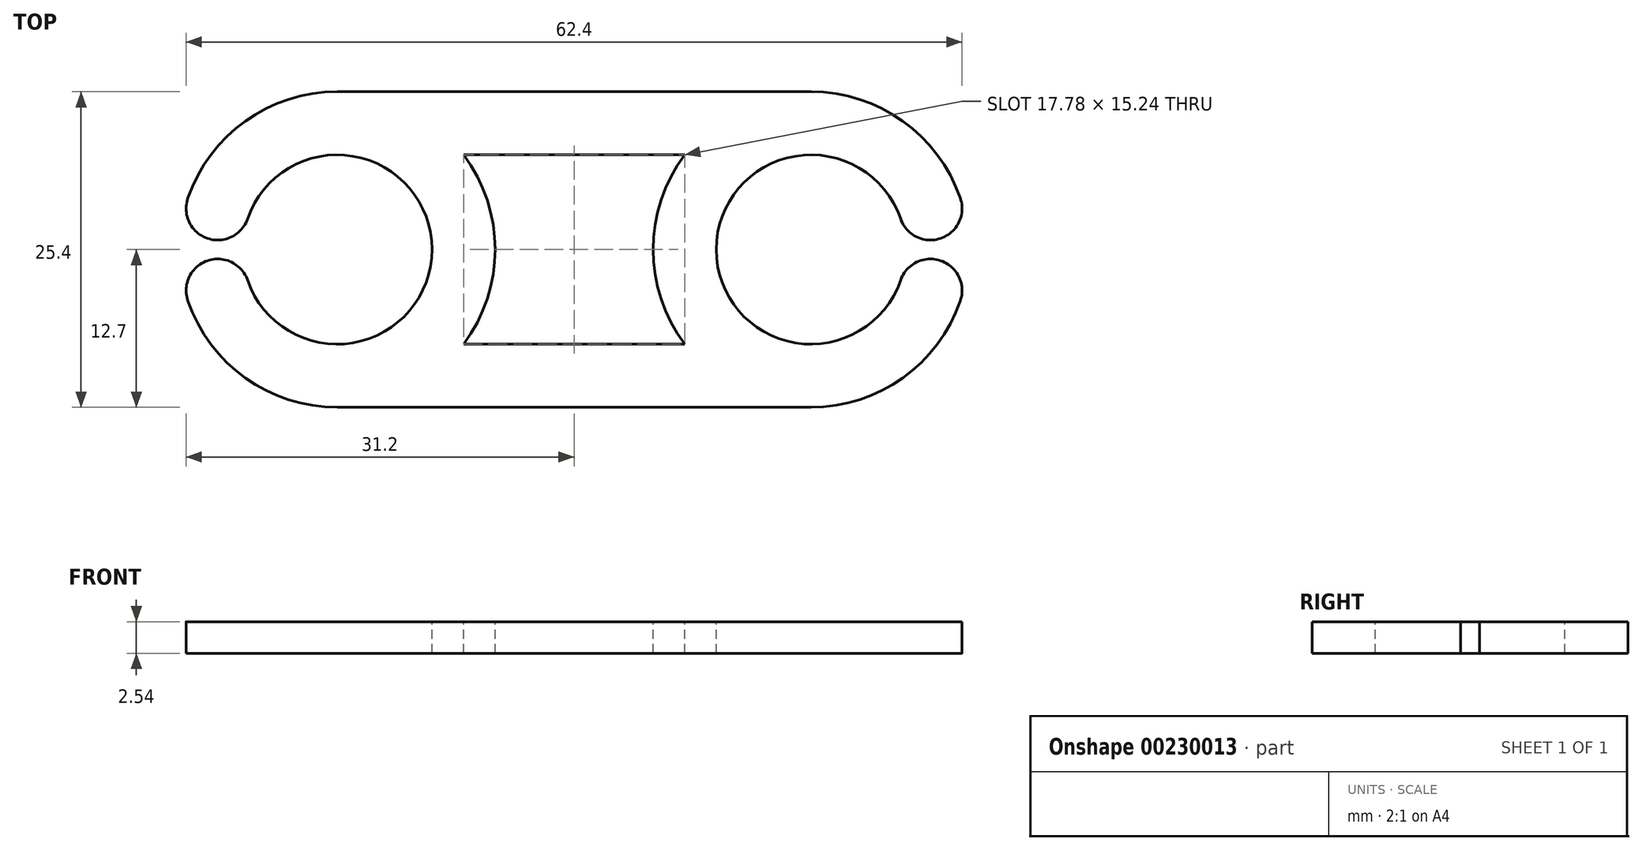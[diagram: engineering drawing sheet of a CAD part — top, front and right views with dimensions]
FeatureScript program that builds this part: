
annotation { "Feature Type Name" : "Feature", "Feature Type Description" : "" }
export const myFeature = defineFeature(function(context is Context, id is Id, definition is map)
    precondition{}
    {
        {
            var Q0;
            Q0=qCreatedBy(makeId("Top.planeOp"),FACE);
            var sketch = newSketch(context, id + "F0", { "sketchPlane" : qUnion([Q0])});
            skArc(sketch, "E0", {"start": v(-19.05, 12.7) * mm, "mid": v(-31.75, 0) * mm, "end": v(-19.05, -12.7) * mm});
            skArc(sketch, "E1", {"start": v(19.05, -12.7) * mm, "mid": v(31.75, 0) * mm, "end": v(19.05, 12.7) * mm});
            skLineSegment(sketch, "E2", {"start": v(-19.05, 12.7) * mm, "end": v(19.05, 12.7) * mm});
            skLineSegment(sketch, "E3", {"start": v(-19.05, -12.7) * mm, "end": v(19.05, -12.7) * mm});
            skLineSegment(sketch, "E4", {"start": v(-19.05, 12.7) * mm, "end": v(-19.05, -12.7) * mm, "construction": true});
            skLineSegment(sketch, "E5", {"start": v(19.05, 12.7) * mm, "end": v(19.05, -12.7) * mm, "construction": true});
            skLineSegment(sketch, "E6", {"start": v(0, 12.7) * mm, "end": v(0, -12.7) * mm, "construction": true});
            skSolve(sketch);
        }
        {
            var Q0;
            Q0 = qSketchRegion(id + "F0", true);
            extrude(context, id + "F1", {"entities" : qUnion([Q0]), "endBound" : BoundingType.SYMMETRIC, "depth" : 2.54 * mm});
        }
        {
            var Q0;
            Q0=makeQuery(id+"F1.opExtrude","CAP_FACE",FACE,{"disambiguationData":[OSD([sQuery(id+"F0.wireOp",EDGE,"E0"),sQuery(id+"F0.wireOp",EDGE,"E1"),sQuery(id+"F0.wireOp",EDGE,"E2"),sQuery(id+"F0.wireOp",EDGE,"E3")])],"isStart":false});
            var sketch = newSketch(context, id + "F2", { "sketchPlane" : qUnion([Q0])});
            skCircle(sketch, "E7", {"center": v(-19.05, 0) * mm, "radius": 7.62 * mm});
            skCircle(sketch, "E8", {"center": v(19.05, 0) * mm, "radius": 7.62 * mm});
            skLineSegment(sketch, "E9", {"start": v(-8.89, 7.62) * mm, "end": v(8.89, 7.62) * mm});
            skLineSegment(sketch, "E10", {"start": v(8.9, -7.62) * mm, "end": v(-8.9, -7.62) * mm});
            skArc(sketch, "E11", {"start": v(8.89, 7.62) * mm, "mid": v(6.35, 0) * mm, "end": v(8.9, -7.62) * mm});
            skArc(sketch, "E12", {"start": v(-8.9, -7.62) * mm, "mid": v(-6.35, 0) * mm, "end": v(-8.89, 7.62) * mm});
            skSolve(sketch);
        }
        {
            var Q0;
            Q0 = qSketchRegion(id + "F2", true);
            extrude(context, id + "F3", {"entities" : qUnion([Q0]), "operationType" : NewBodyOperationType.REMOVE, "oppositeDirection" : true, "depth" : 25.4 * mm});
        }
        {
            var Q0;
            Q0=makeQuery(id+"F1.opExtrude","CAP_FACE",FACE,{"disambiguationData":[OSD([sQuery(id+"F0.wireOp",EDGE,"E0"),sQuery(id+"F0.wireOp",EDGE,"E1"),sQuery(id+"F0.wireOp",EDGE,"E2"),sQuery(id+"F0.wireOp",EDGE,"E3")])],"isStart":false});
            var sketch = newSketch(context, id + "F4", { "sketchPlane" : qUnion([Q0])});
            skCircle(sketch, "E13", {"center": v(0, 0) * mm, "radius": 11.43 * mm});
            skCircle(sketch, "E14", {"center": v(0, 0) * mm, "radius": 6.35 * mm});
            skSolve(sketch);
        }
        {
            var Q0;
            Q0=makeQuery(id+"FMwU1qSj6TiMdTW_1.boolean.opBoolean","MERGE",FACE,{"derivedFrom":[makeQuery(id+"F1.opExtrude","CAP_FACE",FACE,{"disambiguationData":[OSD([sQuery(id+"F0.wireOp",EDGE,"E0"),sQuery(id+"F0.wireOp",EDGE,"E1"),sQuery(id+"F0.wireOp",EDGE,"E2"),sQuery(id+"F0.wireOp",EDGE,"E3")])],"isStart":false}),makeQuery(id+"FMwU1qSj6TiMdTW_1.opExtrude","CAP_FACE",FACE,{"disambiguationData":[OSD([sQuery(id+"F4.wireOp",EDGE,"E13"),sQuery(id+"F4.wireOp",EDGE,"E14")])],"isStart":true})]});
            var sketch = newSketch(context, id + "F5", { "sketchPlane" : qUnion([Q0])});
            skLineSegment(sketch, "E15.bottom", {"start": v(-19.21, 0.76) * mm, "end": v(-31.75, 0.76) * mm});
            skLineSegment(sketch, "E15.top", {"start": v(-19.21, -0.76) * mm, "end": v(-31.75, -0.76) * mm});
            skLineSegment(sketch, "E15.left", {"start": v(-19.21, 0.76) * mm, "end": v(-19.21, -0.76) * mm});
            skLineSegment(sketch, "E15.right", {"start": v(-31.75, 0.76) * mm, "end": v(-31.75, -0.76) * mm});
            skLineSegment(sketch, "E16", {"start": v(-19.05, 0) * mm, "end": v(-31.75, 0) * mm, "construction": true});
            skLineSegment(sketch, "E17.MirrorCS", {"start": v(31.75, 0.76) * mm, "end": v(31.75, -0.76) * mm});
            skLineSegment(sketch, "E18.MirrorCS", {"start": v(19.21, 0.76) * mm, "end": v(19.21, -0.76) * mm});
            skLineSegment(sketch, "E19.MirrorCS", {"start": v(19.05, 0) * mm, "end": v(31.75, 0) * mm, "construction": true});
            skLineSegment(sketch, "E20.MirrorCS", {"start": v(19.21, 0.76) * mm, "end": v(31.75, 0.76) * mm});
            skLineSegment(sketch, "E21.MirrorCS", {"start": v(19.21, -0.76) * mm, "end": v(31.75, -0.76) * mm});
            skSolve(sketch);
        }
        {
            var Q0;
            Q0 = qSketchRegion(id + "F5", true);
            extrude(context, id + "F6", {"entities" : qUnion([Q0]), "operationType" : NewBodyOperationType.REMOVE, "oppositeDirection" : true, "depth" : 25.4 * mm});
        }
        {
            var Q0;
            Q0=makeQuery(id+"F6.boolean.opBoolean","COPY",EDGE,{"derivedFrom":makeQuery(id+"F6.opExtrude","SWEPT_EDGE",EDGE,{"disambiguationData":[OSD([sQuery(id+"F5.wireOp",EDGE,"E17.MirrorCS"),sQuery(id+"F5.wireOp",EDGE,"E20.MirrorCS")])]})});
            var Q1;
            Q1=makeQuery(id+"F6.boolean.opBoolean","INTERSECT",EDGE,{"derivedFrom":[makeQuery(id+"F3.boolean.opBoolean","COPY",FACE,{"derivedFrom":makeQuery(id+"F3.opExtrude","SWEPT_FACE",FACE,{"disambiguationData":[OSD([sQuery(id+"F2.wireOp",EDGE,"E8")])]})}),makeQuery(id+"F6.opExtrude","SWEPT_FACE",FACE,{"disambiguationData":[OSD([sQuery(id+"F5.wireOp",EDGE,"E20.MirrorCS")])]})]});
            var Q2;
            Q2=makeQuery(id+"F6.boolean.opBoolean","COPY",EDGE,{"derivedFrom":makeQuery(id+"F6.opExtrude","SWEPT_EDGE",EDGE,{"disambiguationData":[OSD([sQuery(id+"F5.wireOp",EDGE,"E17.MirrorCS"),sQuery(id+"F5.wireOp",EDGE,"E21.MirrorCS")])]})});
            var Q3;
            Q3=makeQuery(id+"F6.boolean.opBoolean","INTERSECT",EDGE,{"derivedFrom":[makeQuery(id+"F3.boolean.opBoolean","COPY",FACE,{"derivedFrom":makeQuery(id+"F3.opExtrude","SWEPT_FACE",FACE,{"disambiguationData":[OSD([sQuery(id+"F2.wireOp",EDGE,"E8")])]})}),makeQuery(id+"F6.opExtrude","SWEPT_FACE",FACE,{"disambiguationData":[OSD([sQuery(id+"F5.wireOp",EDGE,"E21.MirrorCS")])]})]});
            var Q4;
            Q4=makeQuery(id+"F6.boolean.opBoolean","COPY",EDGE,{"derivedFrom":makeQuery(id+"F6.opExtrude","SWEPT_EDGE",EDGE,{"disambiguationData":[OSD([sQuery(id+"F5.wireOp",EDGE,"E15.bottom"),sQuery(id+"F5.wireOp",EDGE,"E15.right")])]})});
            var Q5;
            Q5=makeQuery(id+"F6.boolean.opBoolean","COPY",EDGE,{"derivedFrom":makeQuery(id+"F6.opExtrude","SWEPT_EDGE",EDGE,{"disambiguationData":[OSD([sQuery(id+"F5.wireOp",EDGE,"E15.top"),sQuery(id+"F5.wireOp",EDGE,"E15.right")])]})});
            var Q6;
            Q6=makeQuery(id+"F6.boolean.opBoolean","INTERSECT",EDGE,{"derivedFrom":[makeQuery(id+"F3.boolean.opBoolean","COPY",FACE,{"derivedFrom":makeQuery(id+"F3.opExtrude","SWEPT_FACE",FACE,{"disambiguationData":[OSD([sQuery(id+"F2.wireOp",EDGE,"E7")])]})}),makeQuery(id+"F6.opExtrude","SWEPT_FACE",FACE,{"disambiguationData":[OSD([sQuery(id+"F5.wireOp",EDGE,"E15.bottom")])]})]});
            var Q7;
            Q7=makeQuery(id+"F6.boolean.opBoolean","INTERSECT",EDGE,{"derivedFrom":[makeQuery(id+"F3.boolean.opBoolean","COPY",FACE,{"derivedFrom":makeQuery(id+"F3.opExtrude","SWEPT_FACE",FACE,{"disambiguationData":[OSD([sQuery(id+"F2.wireOp",EDGE,"E7")])]})}),makeQuery(id+"F6.opExtrude","SWEPT_FACE",FACE,{"disambiguationData":[OSD([sQuery(id+"F5.wireOp",EDGE,"E15.top")])]})]});
            var Q8;
            Q8=makeQuery(id+"F6.boolean.opBoolean","INTERSECT",EDGE,{"derivedFrom":[makeQuery(id+"F1.opExtrude","SWEPT_FACE",FACE,{"disambiguationData":[OSD([sQuery(id+"F0.wireOp",EDGE,"E0")])]}),makeQuery(id+"F6.opExtrude","SWEPT_FACE",FACE,{"disambiguationData":[OSD([sQuery(id+"F5.wireOp",EDGE,"E15.top")])]})]});
            var Q9;
            Q9=makeQuery(id+"F6.boolean.opBoolean","INTERSECT",EDGE,{"derivedFrom":[makeQuery(id+"F1.opExtrude","SWEPT_FACE",FACE,{"disambiguationData":[OSD([sQuery(id+"F0.wireOp",EDGE,"E0")])]}),makeQuery(id+"F6.opExtrude","SWEPT_FACE",FACE,{"disambiguationData":[OSD([sQuery(id+"F5.wireOp",EDGE,"E15.bottom")])]})]});
            var Q10;
            Q10=makeQuery(id+"F6.boolean.opBoolean","INTERSECT",EDGE,{"derivedFrom":[makeQuery(id+"F1.opExtrude","SWEPT_FACE",FACE,{"disambiguationData":[OSD([sQuery(id+"F0.wireOp",EDGE,"E1")])]}),makeQuery(id+"F6.opExtrude","SWEPT_FACE",FACE,{"disambiguationData":[OSD([sQuery(id+"F5.wireOp",EDGE,"E20.MirrorCS")])]})]});
            var Q11;
            Q11=makeQuery(id+"F6.boolean.opBoolean","INTERSECT",EDGE,{"derivedFrom":[makeQuery(id+"F1.opExtrude","SWEPT_FACE",FACE,{"disambiguationData":[OSD([sQuery(id+"F0.wireOp",EDGE,"E1")])]}),makeQuery(id+"F6.opExtrude","SWEPT_FACE",FACE,{"disambiguationData":[OSD([sQuery(id+"F5.wireOp",EDGE,"E21.MirrorCS")])]})]});
            fillet(context, id + "F7", {"entities" : qUnion([Q0, Q1, Q2, Q3, Q4, Q5, Q6, Q7, Q8, Q9, Q10, Q11]), "radius" : 2.54 * mm, "tangentPropagation" : true, "allowEdgeOverflow" : false});
        }
    });
